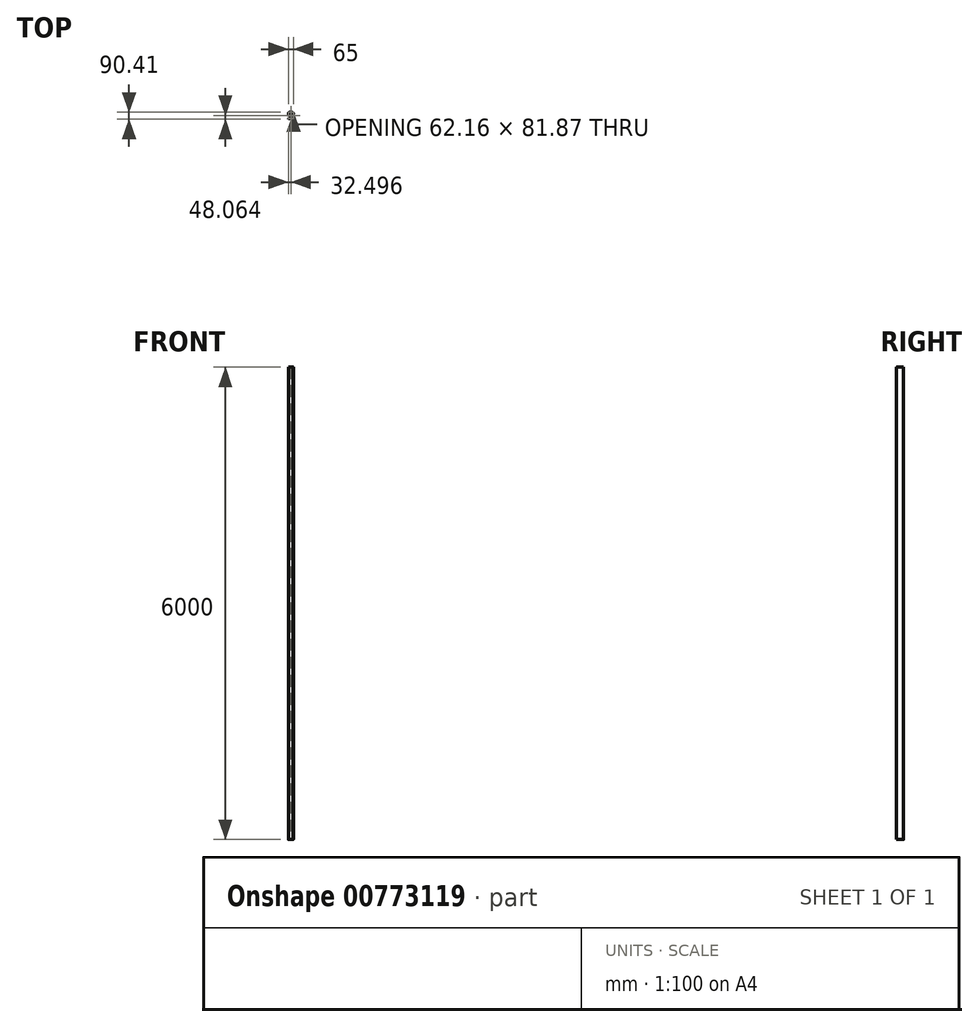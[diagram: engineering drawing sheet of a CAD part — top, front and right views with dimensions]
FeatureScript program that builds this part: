
annotation { "Feature Type Name" : "Feature", "Feature Type Description" : "" }
export const myFeature = defineFeature(function(context is Context, id is Id, definition is map)
    precondition{}
    {
        {
            var Q0;
            Q0=qCreatedBy(makeId("Top.planeOp"),FACE);
            var sketch = newSketch(context, id + "F0", { "sketchPlane" : qUnion([Q0])});
            skArc(sketch, "E0", {"start": v(-199.4, -59.28) * mm, "mid": v(-196.32, -46.4) * mm, "end": v(-200.84, -33.96) * mm});
            skArc(sketch, "E1", {"start": v(-179.28, 5.28) * mm, "mid": v(-190.73, 3.33) * mm, "end": v(-201.85, 0) * mm});
            skArc(sketch, "E2", {"start": v(-201.85, 0) * mm, "mid": v(-211.15, -9.9) * mm, "end": v(-208.79, -23.28) * mm});
            skLineSegment(sketch, "E3", {"start": v(-208.79, -23.28) * mm, "end": v(-200.84, -33.96) * mm});
            skArc(sketch, "E4", {"start": v(-210.26, -78) * mm, "mid": v(-211.56, -81.44) * mm, "end": v(-211.69, -85.12) * mm});
            skLineSegment(sketch, "E5", {"start": v(-199.4, -59.28) * mm, "end": v(-210.26, -78) * mm});
            skLineSegment(sketch, "E6", {"start": v(-179.28, -83.32) * mm, "end": v(-179.28, 15.65) * mm, "construction": true});
            skPoint(sketch, "E7.orphan", {"position": v(-136.35, 0) * mm});
            skArc(sketch, "E8.MirrorCS", {"start": v(-179.28, 5.28) * mm, "mid": v(-167.84, 3.33) * mm, "end": v(-156.72, 0) * mm});
            skArc(sketch, "E9.MirrorCS", {"start": v(-156.72, 0) * mm, "mid": v(-147.41, -9.9) * mm, "end": v(-149.78, -23.28) * mm});
            skLineSegment(sketch, "E10.MirrorCS", {"start": v(-149.78, -23.28) * mm, "end": v(-157.73, -33.96) * mm});
            skArc(sketch, "E11.MirrorCS", {"start": v(-159.17, -59.28) * mm, "mid": v(-162.25, -46.4) * mm, "end": v(-157.73, -33.96) * mm});
            skArc(sketch, "E12.MirrorCS", {"start": v(-148.3, -78) * mm, "mid": v(-147, -81.44) * mm, "end": v(-146.88, -85.12) * mm});
            skLineSegment(sketch, "E13.MirrorCS", {"start": v(-159.17, -59.28) * mm, "end": v(-148.3, -78) * mm});
            skArc(sketch, "E14.0", {"start": v(-209.42, -79.4) * mm, "mid": v(-210.28, -82.2) * mm, "end": v(-210.27, -85.13) * mm});
            skLineSegment(sketch, "E14.1", {"start": v(-198.18, -59.98) * mm, "end": v(-208.64, -78) * mm});
            skLineSegment(sketch, "E14.2", {"start": v(-150.9, -22.45) * mm, "end": v(-158.85, -33.12) * mm});
            skArc(sketch, "E14.3", {"start": v(-160.38, -59.98) * mm, "mid": v(-163.65, -46.32) * mm, "end": v(-158.85, -33.12) * mm});
            skLineSegment(sketch, "E14.4", {"start": v(-160.38, -59.98) * mm, "end": v(-149.93, -78) * mm});
            skArc(sketch, "E14.5", {"start": v(-149.15, -79.4) * mm, "mid": v(-148.3, -82.2) * mm, "end": v(-148.3, -85.13) * mm});
            skArc(sketch, "E14.6", {"start": v(-157.2, -1.31) * mm, "mid": v(-148.76, -10.3) * mm, "end": v(-150.9, -22.45) * mm});
            skArc(sketch, "E14.7", {"start": v(-179.28, 3.87) * mm, "mid": v(-168.08, 1.95) * mm, "end": v(-157.2, -1.31) * mm});
            skArc(sketch, "E14.8", {"start": v(-179.28, 3.87) * mm, "mid": v(-190.48, 1.95) * mm, "end": v(-201.37, -1.31) * mm});
            skArc(sketch, "E14.9", {"start": v(-201.37, -1.31) * mm, "mid": v(-209.81, -10.3) * mm, "end": v(-207.66, -22.45) * mm});
            skLineSegment(sketch, "E14.10", {"start": v(-207.66, -22.45) * mm, "end": v(-199.72, -33.12) * mm});
            skArc(sketch, "E14.11", {"start": v(-198.18, -59.98) * mm, "mid": v(-194.92, -46.32) * mm, "end": v(-199.72, -33.12) * mm});
            skLineSegment(sketch, "E15", {"start": v(-211.69, -85.12) * mm, "end": v(-210.27, -85.13) * mm});
            skLineSegment(sketch, "E16", {"start": v(-148.3, -85.13) * mm, "end": v(-146.88, -85.12) * mm});
            skLineSegment(sketch, "E17", {"start": v(-208.64, -78) * mm, "end": v(-149.93, -78) * mm});
            skLineSegment(sketch, "E18.trimOffspring", {"start": v(-209.42, -79.4) * mm, "end": v(-149.15, -79.4) * mm});
            skPoint(sketch, "E19.orphan", {"position": v(-209.05, -78.7) * mm});
            skSolve(sketch);
        }
        {
            var Q0;
            Q0 = qSketchRegion(id + "F0", true);
            extrude(context, id + "F1", {"entities" : qUnion([Q0]), "depth" : 6000 * mm, "offsetDistance" : 25 * mm});
        }
    });
